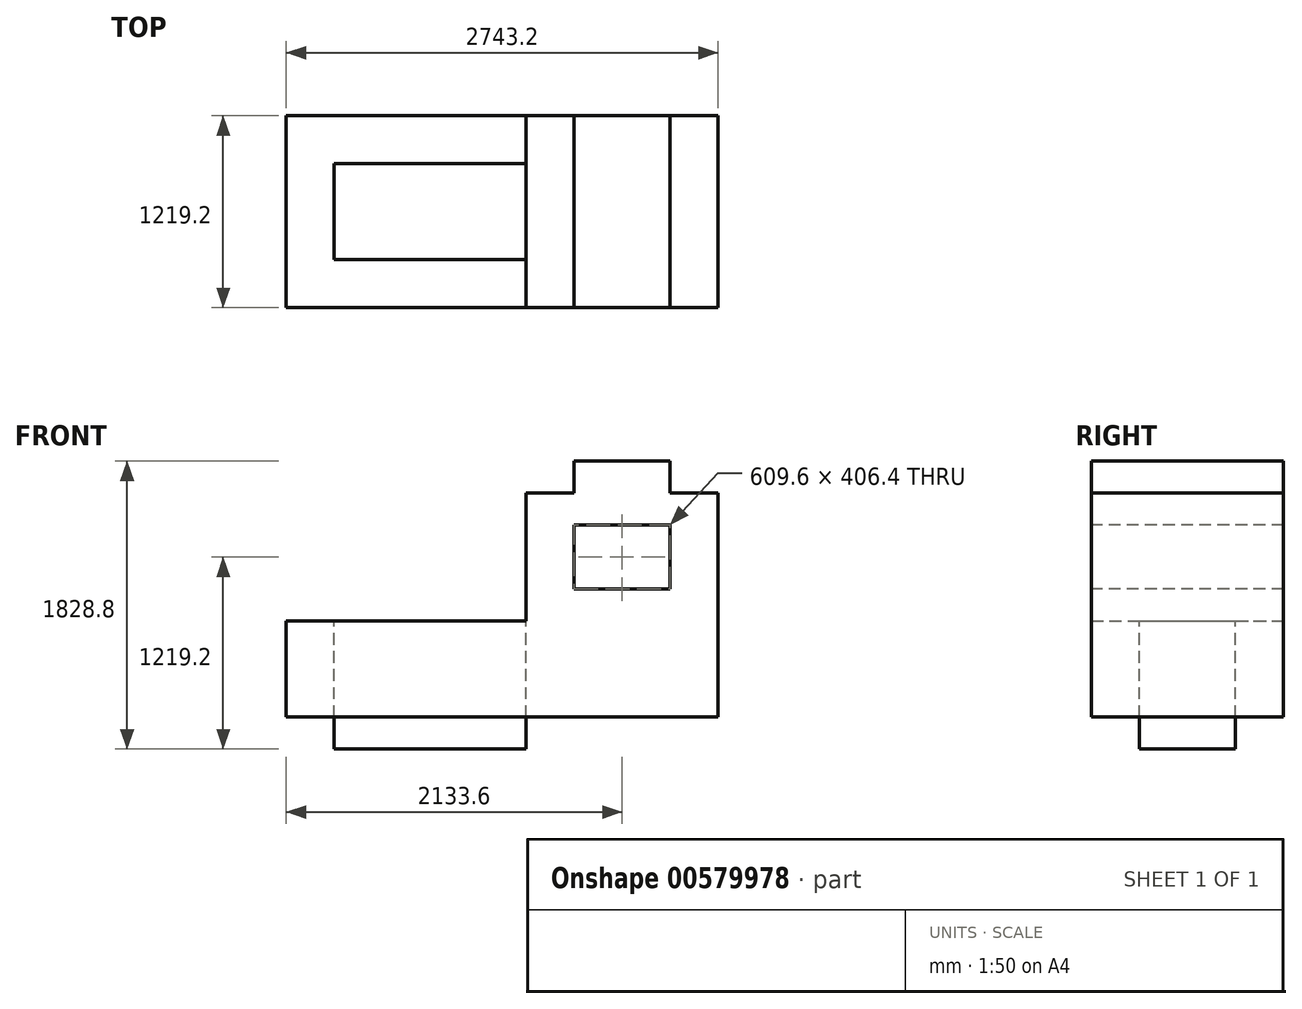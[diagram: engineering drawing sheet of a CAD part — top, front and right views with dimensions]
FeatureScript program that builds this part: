
annotation { "Feature Type Name" : "Feature", "Feature Type Description" : "" }
export const myFeature = defineFeature(function(context is Context, id is Id, definition is map)
    precondition{}
    {
        {
            var Q0;
            Q0=qCreatedBy(makeId("Front.planeOp"),FACE);
            var sketch = newSketch(context, id + "F0", { "sketchPlane" : qUnion([Q0])});
            skLineSegment(sketch, "E0", {"start": v(0, 0) * mm, "end": v(2743.2, 0) * mm});
            skLineSegment(sketch, "E1", {"start": v(2743.2, 0) * mm, "end": v(2743.2, 1422.4) * mm});
            skLineSegment(sketch, "E2", {"start": v(2743.2, 1422.4) * mm, "end": v(2438.4, 1422.4) * mm});
            skLineSegment(sketch, "E3", {"start": v(2438.4, 1422.4) * mm, "end": v(2438.4, 1625.6) * mm});
            skLineSegment(sketch, "E4", {"start": v(2438.4, 1625.6) * mm, "end": v(1828.8, 1625.6) * mm});
            skLineSegment(sketch, "E5", {"start": v(1828.8, 1625.6) * mm, "end": v(1828.8, 1422.4) * mm});
            skLineSegment(sketch, "E6", {"start": v(1828.8, 1422.4) * mm, "end": v(1524, 1422.4) * mm});
            skLineSegment(sketch, "E7", {"start": v(1524, 1422.4) * mm, "end": v(1524, 609.6) * mm});
            skLineSegment(sketch, "E8", {"start": v(1524, 609.6) * mm, "end": v(0, 609.6) * mm});
            skLineSegment(sketch, "E9", {"start": v(0, 609.6) * mm, "end": v(0, 0) * mm});
            skSolve(sketch);
        }
        {
            var Q0;
            Q0=makeQuery(id+"F0.imprint","IMPRINT",FACE,{"disambiguationData":[TD([[makeQuery(id+"F0.imprint","IMPRINT",EDGE,{"derivedFrom":sQuery(id+"F0.wireOp",EDGE,"E0")}),1.0]])]});
            extrude(context, id + "F1", {"entities" : qUnion([Q0]), "depth" : 1219.2 * mm, "offsetDistance" : 25.4 * mm});
        }
        {
            var Q0;
            Q0=makeQuery(id+"F1.opExtrude","CAP_FACE",FACE,{"disambiguationData":[OSD([sQuery(id+"F0.wireOp",EDGE,"E0"),sQuery(id+"F0.wireOp",EDGE,"E1"),sQuery(id+"F0.wireOp",EDGE,"E2"),sQuery(id+"F0.wireOp",EDGE,"E3"),sQuery(id+"F0.wireOp",EDGE,"E4"),sQuery(id+"F0.wireOp",EDGE,"E5"),sQuery(id+"F0.wireOp",EDGE,"E6"),sQuery(id+"F0.wireOp",EDGE,"E7"),sQuery(id+"F0.wireOp",EDGE,"E8"),sQuery(id+"F0.wireOp",EDGE,"E9")])],"isStart":false});
            var sketch = newSketch(context, id + "F2", { "sketchPlane" : qUnion([Q0])});
            skLineSegment(sketch, "E10", {"start": v(1828.8, 1219.2) * mm, "end": v(1828.8, 812.8) * mm});
            skLineSegment(sketch, "E11", {"start": v(1828.8, 812.8) * mm, "end": v(2438.4, 812.8) * mm});
            skLineSegment(sketch, "E12", {"start": v(2438.4, 812.8) * mm, "end": v(2438.4, 1219.2) * mm});
            skLineSegment(sketch, "E13", {"start": v(2438.4, 1219.2) * mm, "end": v(1828.8, 1219.2) * mm});
            skSolve(sketch);
        }
        {
            var Q0;
            Q0=makeQuery(id+"F2.imprint","IMPRINT",FACE,{"disambiguationData":[TD([[makeQuery(id+"F2.imprint","IMPRINT",EDGE,{"derivedFrom":sQuery(id+"F2.wireOp",EDGE,"E10")}),1.0]])]});
            var Q1;
            Q1=sQuery(id+"F2.wireOp",EDGE,"E11");
            var Q2;
            Q2=sQuery(id+"F2.wireOp",EDGE,"E10");
            var Q3;
            Q3=sQuery(id+"F2.wireOp",EDGE,"E13");
            var Q4;
            Q4=sQuery(id+"F2.wireOp",EDGE,"E12");
            extrude(context, id + "F3", {"entities" : qUnion([Q0]), "operationType" : NewBodyOperationType.REMOVE, "surfaceEntities" : qUnion([Q1, Q2, Q3, Q4]), "oppositeDirection" : true, "depth" : 1219.2 * mm, "offsetDistance" : 25.4 * mm});
        }
        {
            var Q0;
            Q0=makeQuery(id+"F1.opExtrude","SWEPT_FACE",FACE,{"disambiguationData":[OSD([sQuery(id+"F0.wireOp",EDGE,"E8")])]});
            var sketch = newSketch(context, id + "F4", { "sketchPlane" : qUnion([Q0])});
            skLineSegment(sketch, "E14", {"start": v(304.8, -304.8) * mm, "end": v(1524, -304.8) * mm});
            skLineSegment(sketch, "E15", {"start": v(1524, -304.8) * mm, "end": v(1524, -914.4) * mm});
            skLineSegment(sketch, "E16", {"start": v(1524, -914.4) * mm, "end": v(304.8, -914.4) * mm});
            skLineSegment(sketch, "E17", {"start": v(304.8, -914.4) * mm, "end": v(304.8, -304.8) * mm});
            skSolve(sketch);
        }
        {
            var Q0;
            Q0 = qSketchRegion(id + "F4", true);
            extrude(context, id + "F5", {"entities" : qUnion([Q0]), "operationType" : NewBodyOperationType.REMOVE, "oppositeDirection" : true, "depth" : 609.6 * mm, "offsetDistance" : 25.4 * mm});
        }
        {
            var Q0;
            Q0=makeQuery(id+"F1.opExtrude","SWEPT_FACE",FACE,{"disambiguationData":[OSD([sQuery(id+"F0.wireOp",EDGE,"E0")])]});
            var sketch = newSketch(context, id + "F6", { "sketchPlane" : qUnion([Q0])});
            skLineSegment(sketch, "E18", {"start": v(304.8, 914.4) * mm, "end": v(304.8, 304.8) * mm});
            skLineSegment(sketch, "E19", {"start": v(304.8, 304.8) * mm, "end": v(1524, 304.8) * mm});
            skLineSegment(sketch, "E20", {"start": v(1524, 304.8) * mm, "end": v(1524, 914.4) * mm});
            skLineSegment(sketch, "E21", {"start": v(1524, 914.4) * mm, "end": v(304.8, 914.4) * mm});
            skSolve(sketch);
        }
        {
            var Q0;
            Q0=makeQuery(id+"F6.imprint","IMPRINT",FACE,{"disambiguationData":[TD([[makeQuery(id+"F6.imprint","IMPRINT",EDGE,{"derivedFrom":sQuery(id+"F6.wireOp",EDGE,"E18")}),1.0]])]});
            extrude(context, id + "F7", {"entities" : qUnion([Q0]), "operationType" : NewBodyOperationType.ADD, "depth" : 203.2 * mm, "offsetDistance" : 25.4 * mm});
        }
    });
